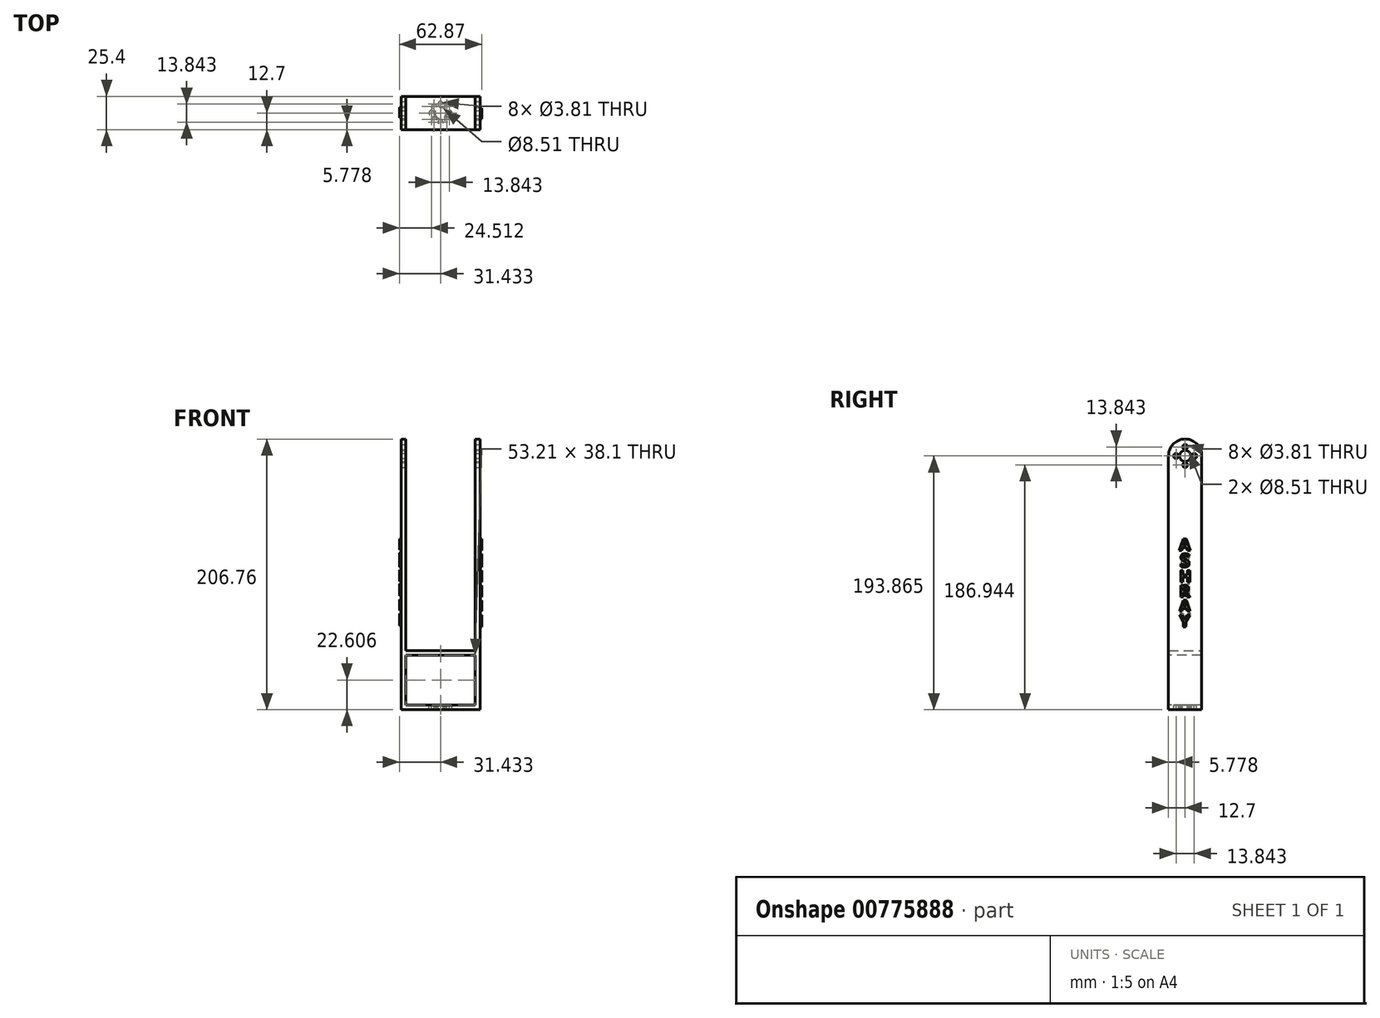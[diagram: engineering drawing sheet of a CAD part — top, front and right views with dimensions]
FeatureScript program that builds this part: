
annotation { "Feature Type Name" : "Feature", "Feature Type Description" : "" }
export const myFeature = defineFeature(function(context is Context, id is Id, definition is map)
    precondition{}
    {
        {
            var Q0;
            Q0=qCreatedBy(makeId("Top.planeOp"),FACE);
            var sketch = newSketch(context, id + "F0", { "sketchPlane" : qUnion([Q0])});
            skLineSegment(sketch, "E0.bottom", {"start": v(-26.29, 12.7) * mm, "end": v(34.04, 12.7) * mm});
            skLineSegment(sketch, "E0.top", {"start": v(-26.29, -12.7) * mm, "end": v(34.04, -12.7) * mm});
            skLineSegment(sketch, "E0.left", {"start": v(-26.29, 12.7) * mm, "end": v(-26.29, -12.7) * mm});
            skLineSegment(sketch, "E0.right", {"start": v(34.04, 12.7) * mm, "end": v(34.04, -12.7) * mm});
            skSolve(sketch);
        }
        {
            var Q0;
            Q0=makeQuery(id+"F0.imprint","IMPRINT",FACE,{"disambiguationData":[TD([[makeQuery(id+"F0.imprint","IMPRINT",EDGE,{"derivedFrom":sQuery(id+"F0.wireOp",EDGE,"E0.bottom")}),-1.0]])]});
            extrude(context, id + "F1", {"entities" : qUnion([Q0]), "depth" : 3.56 * mm});
        }
        {
            var Q0;
            Q0=makeQuery(id+"F1.opExtrude","CAP_FACE",FACE,{"disambiguationData":[OSD([sQuery(id+"F0.wireOp",EDGE,"E0.bottom"),sQuery(id+"F0.wireOp",EDGE,"E0.top"),sQuery(id+"F0.wireOp",EDGE,"E0.left"),sQuery(id+"F0.wireOp",EDGE,"E0.right")])],"isStart":false});
            var sketch = newSketch(context, id + "F2", { "sketchPlane" : qUnion([Q0])});
            skLineSegment(sketch, "E1.bottom", {"start": v(-26.29, 12.7) * mm, "end": v(-22.73, 12.7) * mm});
            skLineSegment(sketch, "E1.top", {"start": v(-26.29, -12.7) * mm, "end": v(-22.73, -12.7) * mm});
            skLineSegment(sketch, "E1.left", {"start": v(-26.29, 12.7) * mm, "end": v(-26.29, -12.7) * mm});
            skLineSegment(sketch, "E1.right", {"start": v(-22.73, 12.7) * mm, "end": v(-22.73, -12.7) * mm});
            skLineSegment(sketch, "E2.bottom", {"start": v(34.04, 12.7) * mm, "end": v(30.48, 12.7) * mm});
            skLineSegment(sketch, "E2.top", {"start": v(34.04, -12.7) * mm, "end": v(30.48, -12.7) * mm});
            skLineSegment(sketch, "E2.left", {"start": v(34.04, 12.7) * mm, "end": v(34.04, -12.7) * mm});
            skLineSegment(sketch, "E2.right", {"start": v(30.48, 12.7) * mm, "end": v(30.48, -12.7) * mm});
            skSolve(sketch);
        }
        {
            var Q0;
            Q0=makeQuery(id+"F2.imprint","IMPRINT",FACE,{"disambiguationData":[TD([[makeQuery(id+"F2.imprint","IMPRINT",EDGE,{"derivedFrom":sQuery(id+"F2.wireOp",EDGE,"E1.bottom")}),-1.0]])]});
            var Q1;
            Q1=makeQuery(id+"F2.imprint","IMPRINT",FACE,{"disambiguationData":[TD([[makeQuery(id+"F2.imprint","IMPRINT",EDGE,{"derivedFrom":sQuery(id+"F2.wireOp",EDGE,"E2.bottom")}),-1.0]])]});
            extrude(context, id + "F3", {"entities" : qUnion([Q0, Q1]), "operationType" : NewBodyOperationType.ADD, "depth" : 203.2 * mm});
        }
        {
            var Q0;
            Q0=makeQuery(id+"F3.opExtrude","CAP_EDGE",EDGE,{"disambiguationData":[OSD([sQuery(id+"F2.wireOp",EDGE,"E2.bottom")])],"isStart":false});
            fillet(context, id + "F4", {"entities" : qUnion([Q0]), "radius" : 12.7 * mm, "tangentPropagation" : true, "allowEdgeOverflow" : false});
        }
        {
            var Q0;
            Q0=makeQuery(id+"F3.opExtrude","CAP_EDGE",EDGE,{"disambiguationData":[OSD([sQuery(id+"F2.wireOp",EDGE,"E2.top")])],"isStart":false});
            var Q1;
            Q1=makeQuery(id+"F3.opExtrude","CAP_EDGE",EDGE,{"disambiguationData":[OSD([sQuery(id+"F2.wireOp",EDGE,"E1.top")])],"isStart":false});
            var Q2;
            Q2=makeQuery(id+"F3.opExtrude","CAP_EDGE",EDGE,{"disambiguationData":[OSD([sQuery(id+"F2.wireOp",EDGE,"E1.bottom")])],"isStart":false});
            fillet(context, id + "F5", {"entities" : qUnion([Q0, Q1, Q2]), "radius" : 12.7 * mm, "tangentPropagation" : true, "allowEdgeOverflow" : false});
        }
        {
            var Q0;
            Q0=makeQuery(id+"F3.boolean.opBoolean","MERGE",FACE,{"derivedFrom":[makeQuery(id+"F1.opExtrude","SWEPT_FACE",FACE,{"disambiguationData":[OSD([sQuery(id+"F0.wireOp",EDGE,"E0.right")])]}),makeQuery(id+"F3.opExtrude","SWEPT_FACE",FACE,{"disambiguationData":[OSD([sQuery(id+"F2.wireOp",EDGE,"E2.left")])]})]});
            var sketch = newSketch(context, id + "F6", { "sketchPlane" : qUnion([Q0])});
            skCircle(sketch, "E3", {"center": v(0, 200.79) * mm, "radius": 1.9 * mm});
            skCircle(sketch, "E4", {"center": v(0, 186.94) * mm, "radius": 1.9 * mm});
            skCircle(sketch, "E5", {"center": v(0, 193.87) * mm, "radius": 4.25 * mm});
            skCircle(sketch, "E6", {"center": v(6.92, 193.87) * mm, "radius": 1.9 * mm});
            skCircle(sketch, "E7", {"center": v(-6.92, 193.87) * mm, "radius": 1.9 * mm});
            skSolve(sketch);
        }
        {
            var Q0;
            Q0=makeQuery(id+"F6.imprint","IMPRINT",FACE,{"disambiguationData":[TD([[makeQuery(id+"F6.imprint","IMPRINT",EDGE,{"derivedFrom":sQuery(id+"F6.wireOp",EDGE,"E5")}),1.0]])]});
            var Q1;
            Q1=makeQuery(id+"F6.imprint","IMPRINT",FACE,{"disambiguationData":[TD([[makeQuery(id+"F6.imprint","IMPRINT",EDGE,{"derivedFrom":sQuery(id+"F6.wireOp",EDGE,"E3")}),1.0]])]});
            var Q2;
            Q2=makeQuery(id+"F6.imprint","IMPRINT",FACE,{"disambiguationData":[TD([[makeQuery(id+"F6.imprint","IMPRINT",EDGE,{"derivedFrom":sQuery(id+"F6.wireOp",EDGE,"E7")}),1.0]])]});
            var Q3;
            Q3=makeQuery(id+"F6.imprint","IMPRINT",FACE,{"disambiguationData":[TD([[makeQuery(id+"F6.imprint","IMPRINT",EDGE,{"derivedFrom":sQuery(id+"F6.wireOp",EDGE,"E4")}),1.0]])]});
            var Q4;
            Q4=makeQuery(id+"F6.imprint","IMPRINT",FACE,{"disambiguationData":[TD([[makeQuery(id+"F6.imprint","IMPRINT",EDGE,{"derivedFrom":sQuery(id+"F6.wireOp",EDGE,"E6")}),1.0]])]});
            extrude(context, id + "F7", {"entities" : qUnion([Q0, Q1, Q2, Q3, Q4]), "operationType" : NewBodyOperationType.REMOVE, "oppositeDirection" : true, "depth" : 254 * mm});
        }
        {
            var Q0;
            Q0=makeQuery(id+"F1.opExtrude","CAP_FACE",FACE,{"disambiguationData":[OSD([sQuery(id+"F0.wireOp",EDGE,"E0.bottom"),sQuery(id+"F0.wireOp",EDGE,"E0.top"),sQuery(id+"F0.wireOp",EDGE,"E0.left"),sQuery(id+"F0.wireOp",EDGE,"E0.right")])],"isStart":false});
            var sketch = newSketch(context, id + "F8", { "sketchPlane" : qUnion([Q0])});
            skCircle(sketch, "E8", {"center": v(3.87, 0) * mm, "radius": 4.25 * mm});
            skCircle(sketch, "E9", {"center": v(3.87, 6.92) * mm, "radius": 1.9 * mm});
            skCircle(sketch, "E10", {"center": v(10.8, 0) * mm, "radius": 1.9 * mm});
            skCircle(sketch, "E11", {"center": v(3.87, -6.92) * mm, "radius": 1.9 * mm});
            skCircle(sketch, "E12", {"center": v(-3.05, 0) * mm, "radius": 1.9 * mm});
            skCircle(sketch, "E13", {"center": v(-1.02, -4.9) * mm, "radius": 1.9 * mm});
            skCircle(sketch, "E14", {"center": v(8.77, -4.9) * mm, "radius": 1.9 * mm});
            skCircle(sketch, "E15", {"center": v(8.77, 4.9) * mm, "radius": 1.9 * mm});
            skCircle(sketch, "E16", {"center": v(-1.02, 4.9) * mm, "radius": 1.9 * mm});
            skLineSegment(sketch, "E17", {"start": v(-1.02, -4.9) * mm, "end": v(3.87, 0) * mm});
            skLineSegment(sketch, "E18", {"start": v(3.87, 0) * mm, "end": v(8.77, -4.9) * mm});
            skLineSegment(sketch, "E19", {"start": v(3.87, 0) * mm, "end": v(8.77, 4.9) * mm});
            skLineSegment(sketch, "E20", {"start": v(3.87, 0) * mm, "end": v(-1.02, 4.9) * mm});
            skSolve(sketch);
        }
        {
            var Q0;
            Q0=makeQuery(id+"F3.opExtrude","SWEPT_FACE",FACE,{"disambiguationData":[OSD([sQuery(id+"F2.wireOp",EDGE,"E2.right")])]});
            var sketch = newSketch(context, id + "F9", { "sketchPlane" : qUnion([Q0])});
            skLineSegment(sketch, "E21.bottom", {"start": v(12.7, 152.15) * mm, "end": v(-12.7, 152.15) * mm});
            skLineSegment(sketch, "E21.top", {"start": v(12.7, 148.6) * mm, "end": v(-12.7, 148.6) * mm});
            skLineSegment(sketch, "E21.left", {"start": v(12.7, 152.15) * mm, "end": v(12.7, 148.6) * mm});
            skLineSegment(sketch, "E21.right", {"start": v(-12.7, 152.15) * mm, "end": v(-12.7, 148.6) * mm});
            skSolve(sketch);
        }
        {
            var Q0;
            Q0=makeQuery(id+"F3.boolean.opBoolean","MERGE",FACE,{"derivedFrom":[makeQuery(id+"F1.opExtrude","SWEPT_FACE",FACE,{"disambiguationData":[OSD([sQuery(id+"F0.wireOp",EDGE,"E0.left")])]}),makeQuery(id+"F3.opExtrude","SWEPT_FACE",FACE,{"disambiguationData":[OSD([sQuery(id+"F2.wireOp",EDGE,"E1.left")])]})]});
            var sketch = newSketch(context, id + "F10", { "sketchPlane" : qUnion([Q0])});
            skText(sketch, "E22", { "text": "A", "fontName": "OpenSans-Bold.ttf"});
            skText(sketch, "E23", { "text": "H", "fontName": "OpenSans-Bold.ttf"});
            skText(sketch, "E24", { "text": "R", "fontName": "OpenSans-Bold.ttf"});
            skText(sketch, "E25", { "text": "A", "fontName": "OpenSans-Bold.ttf"});
            skText(sketch, "E26", { "text": "Y", "fontName": "OpenSans-Bold.ttf"});
            skText(sketch, "E27", { "text": "S", "fontName": "OpenSans-Bold.ttf"});
            const initialGuessF10  = {"E22": [-0.00444, 0.12208, 1, 0, 0.00848], "E23": [-0.00444, 0.09818, 1, 0, 0.00865], "E24": [-0.00444, 0.08682, 1, 0, 0.00883], "E25": [-0.00444, 0.0758, 1, 0, 0.00848], "E26": [-0.00444, 0.06397, 1, 0, 0.0093], "E27": [-0.00406, 0.10938, 1, 0, 0.01016]};
            skSetInitialGuess(sketch, initialGuessF10);
            skSolve(sketch);
        }
        {
            var Q0;
            Q0=makeQuery(id+"F10.imprint","IMPRINT",FACE,{"disambiguationData":[TD([[makeQuery(id+"F10.imprint","IMPRINT",EDGE,{"derivedFrom":sQuery(id+"F10.wireOp",EDGE,"E22.sketch_text.stroke-0")}),-1.0]])]});
            var Q1;
            Q1=makeQuery(id+"F10.imprint","IMPRINT",FACE,{"disambiguationData":[TD([[makeQuery(id+"F10.imprint","IMPRINT",EDGE,{"derivedFrom":sQuery(id+"F10.wireOp",EDGE,"E27.sketch_text.stroke-0")}),-1.0]])]});
            var Q2;
            Q2=makeQuery(id+"F10.imprint","IMPRINT",FACE,{"disambiguationData":[TD([[makeQuery(id+"F10.imprint","IMPRINT",EDGE,{"derivedFrom":sQuery(id+"F10.wireOp",EDGE,"E23.sketch_text.stroke-0")}),-1.0]])]});
            var Q3;
            Q3=makeQuery(id+"F10.imprint","IMPRINT",FACE,{"disambiguationData":[TD([[makeQuery(id+"F10.imprint","IMPRINT",EDGE,{"derivedFrom":sQuery(id+"F10.wireOp",EDGE,"E24.sketch_text.stroke-0")}),-1.0]])]});
            var Q4;
            Q4=makeQuery(id+"F10.imprint","IMPRINT",FACE,{"disambiguationData":[TD([[makeQuery(id+"F10.imprint","IMPRINT",EDGE,{"derivedFrom":sQuery(id+"F10.wireOp",EDGE,"E25.sketch_text.stroke-0")}),-1.0]])]});
            var Q5;
            Q5=makeQuery(id+"F10.imprint","IMPRINT",FACE,{"disambiguationData":[TD([[makeQuery(id+"F10.imprint","IMPRINT",EDGE,{"derivedFrom":sQuery(id+"F10.wireOp",EDGE,"E26.sketch_text.stroke-0")}),-1.0]])]});
            extrude(context, id + "F11", {"entities" : qUnion([Q0, Q1, Q2, Q3, Q4, Q5]), "operationType" : NewBodyOperationType.ADD, "depth" : 1.27 * mm});
        }
        {
            var Q0;
            Q0=makeQuery(id+"FYo4dK7PWjSjNg0_1.boolean.opBoolean","SPLIT",FACE,{"disambiguationData":[TD([makeQuery(id+"FYo4dK7PWjSjNg0_1.opExtrude","SWEPT_FACE",FACE,{"disambiguationData":[OSD([sQuery(id+"F9.wireOp",EDGE,"E21.top")])]})])],"derivedFrom":makeQuery(id+"F3.opExtrude","SWEPT_FACE",FACE,{"disambiguationData":[OSD([sQuery(id+"F2.wireOp",EDGE,"E1.right")])]})});
            var sketch = newSketch(context, id + "F12", { "sketchPlane" : qUnion([Q0])});
            skLineSegment(sketch, "E28.bottom", {"start": v(12.7, 45.21) * mm, "end": v(-12.7, 45.21) * mm});
            skLineSegment(sketch, "E28.top", {"start": v(12.7, 41.66) * mm, "end": v(-12.7, 41.66) * mm});
            skLineSegment(sketch, "E28.left", {"start": v(12.7, 45.21) * mm, "end": v(12.7, 41.66) * mm});
            skLineSegment(sketch, "E28.right", {"start": v(-12.7, 45.21) * mm, "end": v(-12.7, 41.66) * mm});
            skSolve(sketch);
        }
        {
            var Q0;
            Q0=makeQuery(id+"F12.imprint","IMPRINT",FACE,{"disambiguationData":[TD([[makeQuery(id+"F12.imprint","IMPRINT",EDGE,{"derivedFrom":sQuery(id+"F12.wireOp",EDGE,"E28.bottom")}),1.0]])]});
            extrude(context, id + "F13", {"entities" : qUnion([Q0]), "operationType" : NewBodyOperationType.ADD, "depth" : 53.34 * mm});
        }
        {
            var Q0;
            Q0=makeQuery(id+"F8.imprint","IMPRINT",FACE,{"disambiguationData":[TD([[makeQuery(id+"F8.imprint","IMPRINT",EDGE,{"derivedFrom":sQuery(id+"F8.wireOp",EDGE,"E15")}),1.0]])]});
            var Q1;
            Q1=makeQuery(id+"F8.imprint","IMPRINT",FACE,{"disambiguationData":[TD([[makeQuery(id+"F8.imprint","IMPRINT",EDGE,{"derivedFrom":sQuery(id+"F8.wireOp",EDGE,"E10")}),1.0]])]});
            var Q2;
            Q2=makeQuery(id+"F8.imprint","IMPRINT",FACE,{"disambiguationData":[TD([[makeQuery(id+"F8.imprint","IMPRINT",EDGE,{"derivedFrom":sQuery(id+"F8.wireOp",EDGE,"E14")}),1.0]])]});
            var Q3;
            Q3=makeQuery(id+"F8.imprint","IMPRINT",FACE,{"disambiguationData":[TD([[makeQuery(id+"F8.imprint","IMPRINT",EDGE,{"derivedFrom":sQuery(id+"F8.wireOp",EDGE,"E11")}),1.0]])]});
            var Q4;
            Q4=makeQuery(id+"F8.imprint","IMPRINT",FACE,{"disambiguationData":[TD([[makeQuery(id+"F8.imprint","IMPRINT",EDGE,{"derivedFrom":sQuery(id+"F8.wireOp",EDGE,"E13")}),1.0]])]});
            var Q5;
            Q5=makeQuery(id+"F8.imprint","IMPRINT",FACE,{"disambiguationData":[TD([[makeQuery(id+"F8.imprint","IMPRINT",EDGE,{"derivedFrom":sQuery(id+"F8.wireOp",EDGE,"E12")}),1.0]])]});
            var Q6;
            Q6=makeQuery(id+"F8.imprint","IMPRINT",FACE,{"disambiguationData":[TD([[makeQuery(id+"F8.imprint","IMPRINT",EDGE,{"derivedFrom":sQuery(id+"F8.wireOp",EDGE,"E16")}),1.0]])]});
            var Q7;
            Q7=makeQuery(id+"F8.imprint","IMPRINT",FACE,{"disambiguationData":[TD([[makeQuery(id+"F8.imprint","IMPRINT",EDGE,{"derivedFrom":sQuery(id+"F8.wireOp",EDGE,"E9")}),1.0]])]});
            var Q8;
            {var subQ0=sQuery(id+"F8.wireOp",EDGE,"E20");var subQ1=sQuery(id+"F8.wireOp",EDGE,"E8");var subQ2=makeQuery(id+"F8.imprint","INTERSECT",VERTEX,{"derivedFrom":[subQ1,subQ0]});Q8=makeQuery(id+"F8.imprint","IMPRINT",FACE,{"disambiguationData":[TD([[makeQuery(id+"F8.imprint","IMPRINT",EDGE,{"disambiguationData":[TD([[subQ2,1.0]])],"derivedFrom":subQ1}),1.0]])]});}
            var Q9;
            {var subQ0=sQuery(id+"F8.wireOp",EDGE,"E20");var subQ1=sQuery(id+"F8.wireOp",EDGE,"E8");var subQ2=makeQuery(id+"F8.imprint","INTERSECT",VERTEX,{"derivedFrom":[subQ1,subQ0]});Q9=makeQuery(id+"F8.imprint","IMPRINT",FACE,{"disambiguationData":[TD([[makeQuery(id+"F8.imprint","IMPRINT",EDGE,{"disambiguationData":[TD([[subQ2,-1.0]])],"derivedFrom":subQ1}),1.0]])]});}
            var Q10;
            {var subQ0=sQuery(id+"F8.wireOp",EDGE,"E17");var subQ1=sQuery(id+"F8.wireOp",EDGE,"E8");var subQ2=makeQuery(id+"F8.imprint","INTERSECT",VERTEX,{"derivedFrom":[subQ1,subQ0]});Q10=makeQuery(id+"F8.imprint","IMPRINT",FACE,{"disambiguationData":[TD([[makeQuery(id+"F8.imprint","IMPRINT",EDGE,{"disambiguationData":[TD([[subQ2,-1.0]])],"derivedFrom":subQ1}),1.0]])]});}
            var Q11;
            {var subQ0=sQuery(id+"F8.wireOp",EDGE,"E19");var subQ1=sQuery(id+"F8.wireOp",EDGE,"E8");var subQ2=makeQuery(id+"F8.imprint","INTERSECT",VERTEX,{"derivedFrom":[subQ1,subQ0]});Q11=makeQuery(id+"F8.imprint","IMPRINT",FACE,{"disambiguationData":[TD([[makeQuery(id+"F8.imprint","IMPRINT",EDGE,{"disambiguationData":[TD([[subQ2,1.0]])],"derivedFrom":subQ1}),1.0]])]});}
            extrude(context, id + "F14", {"entities" : qUnion([Q0, Q1, Q2, Q3, Q4, Q5, Q6, Q7, Q8, Q9, Q10, Q11]), "operationType" : NewBodyOperationType.REMOVE, "oppositeDirection" : true, "depth" : 25.4 * mm});
        }
        {
            var Q0;
            Q0=makeQuery(id+"F3.boolean.opBoolean","MERGE",FACE,{"derivedFrom":[makeQuery(id+"F1.opExtrude","SWEPT_FACE",FACE,{"disambiguationData":[OSD([sQuery(id+"F0.wireOp",EDGE,"E0.right")])]}),makeQuery(id+"F3.opExtrude","SWEPT_FACE",FACE,{"disambiguationData":[OSD([sQuery(id+"F2.wireOp",EDGE,"E2.left")])]})]});
            var sketch = newSketch(context, id + "F15", { "sketchPlane" : qUnion([Q0])});
            skText(sketch, "E29", { "text": "A", "fontName": "OpenSans-Bold.ttf"});
            skText(sketch, "E30", { "text": "S", "fontName": "OpenSans-Bold.ttf"});
            skText(sketch, "E31", { "text": "H", "fontName": "OpenSans-Bold.ttf"});
            skText(sketch, "E32", { "text": "R", "fontName": "OpenSans-Bold.ttf"});
            skText(sketch, "E33", { "text": "A", "fontName": "OpenSans-Bold.ttf"});
            skText(sketch, "E34", { "text": "Y", "fontName": "OpenSans-Bold.ttf"});
            const initialGuessF15  = {"E29": [-0.00466, 0.12167, 1, 0, 0.0089], "E30": [-0.00406, 0.10897, 1, 0, 0.01016], "E31": [-0.00457, 0.09754, 1, 0, 0.0089], "E32": [-0.00448, 0.0861, 1, 0, 0.0089], "E33": [-0.00444, 0.07509, 1, 0, 0.00848], "E34": [-0.00444, 0.06326, 1, 0, 0.0093]};
            skSetInitialGuess(sketch, initialGuessF15);
            skSolve(sketch);
        }
        {
            var Q0;
            Q0=makeQuery(id+"F15.imprint","IMPRINT",FACE,{"disambiguationData":[TD([[makeQuery(id+"F15.imprint","IMPRINT",EDGE,{"derivedFrom":sQuery(id+"F15.wireOp",EDGE,"E29.sketch_text.stroke-0")}),-1.0]])]});
            var Q1;
            Q1=makeQuery(id+"F15.imprint","IMPRINT",FACE,{"disambiguationData":[TD([[makeQuery(id+"F15.imprint","IMPRINT",EDGE,{"derivedFrom":sQuery(id+"F15.wireOp",EDGE,"E30.sketch_text.stroke-0")}),-1.0]])]});
            var Q2;
            Q2=makeQuery(id+"F15.imprint","IMPRINT",FACE,{"disambiguationData":[TD([[makeQuery(id+"F15.imprint","IMPRINT",EDGE,{"derivedFrom":sQuery(id+"F15.wireOp",EDGE,"E31.sketch_text.stroke-0")}),-1.0]])]});
            var Q3;
            Q3=makeQuery(id+"F15.imprint","IMPRINT",FACE,{"disambiguationData":[TD([[makeQuery(id+"F15.imprint","IMPRINT",EDGE,{"derivedFrom":sQuery(id+"F15.wireOp",EDGE,"E32.sketch_text.stroke-0")}),-1.0]])]});
            var Q4;
            Q4=makeQuery(id+"F15.imprint","IMPRINT",FACE,{"disambiguationData":[TD([[makeQuery(id+"F15.imprint","IMPRINT",EDGE,{"derivedFrom":sQuery(id+"F15.wireOp",EDGE,"E33.sketch_text.stroke-0")}),-1.0]])]});
            var Q5;
            Q5=makeQuery(id+"F15.imprint","IMPRINT",FACE,{"disambiguationData":[TD([[makeQuery(id+"F15.imprint","IMPRINT",EDGE,{"derivedFrom":sQuery(id+"F15.wireOp",EDGE,"E34.sketch_text.stroke-0")}),-1.0]])]});
            extrude(context, id + "F16", {"entities" : qUnion([Q0, Q1, Q2, Q3, Q4, Q5]), "operationType" : NewBodyOperationType.ADD, "depth" : 1.27 * mm});
        }
    });
